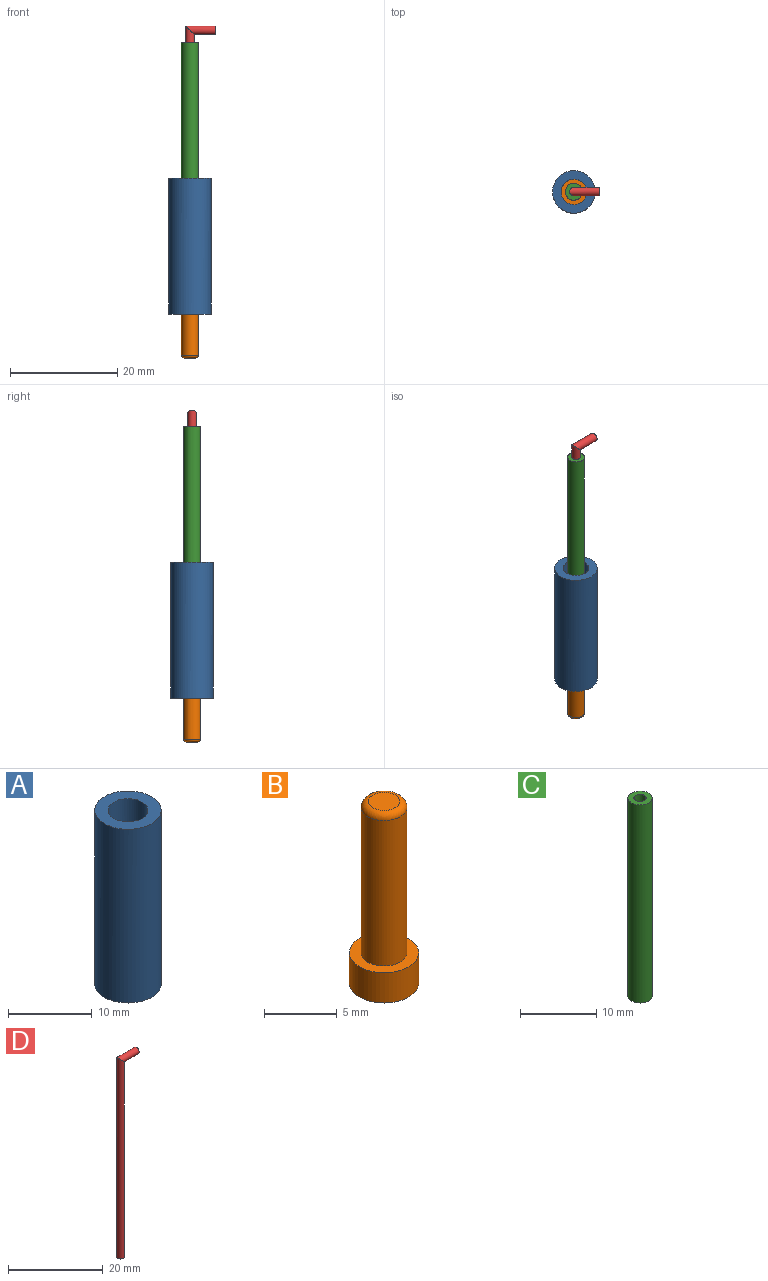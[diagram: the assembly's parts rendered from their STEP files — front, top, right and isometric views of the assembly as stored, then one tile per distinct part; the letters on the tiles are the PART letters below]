
ASSEMBLY  parts=4 mates=3
PART A: 6 faces, bbox 7.9x7.9x25.4 mm
  f0: cylinder r=2.38mm len=22.86mm, axis (0,0,-1), area 342mm2, adj f2,f4
  f1: cylinder r=3.97mm len=25.4mm, axis (0,0,-1), area 633.4mm2, adj f2,f3
  f2: plane 7.94x7.94mm, normal (0,0,1), area 31.7mm2, adj f0,f1
  f3: plane 7.94x7.94mm, normal (0,0,-1), area 41.6mm2, adj f1,f5
  f4: plane 4.76x4.76mm, normal (0,0,1), area 9.9mm2, adj f0,f5
  f5: cylinder r=1.59mm len=3.18mm, axis (0,0,-1), area 25.3mm2, adj f3,f4
PART B: 8 faces, bbox 4.8x4.8x15.2 mm
  f0: cylinder r=2.37mm len=4.75mm, axis (0,0,-1), area 37.9mm2, adj f1,f2
  f1: plane 4.75x4.75mm, normal (0,0,1), area 9.9mm2, adj f0,f3
  f2: plane 4.75x4.75mm, normal (0,0,-1), area 15.7mm2, adj f0,f6
  f3: cylinder r=1.57mm len=12.19mm, axis (0,0,-1), area 120.6mm2, adj f1,f5
  f4: plane 2.13x2.13mm, normal (0,0,1), area 3.6mm2, adj f5
  f5: torus R=1.07mm, axis (0,0,1), area 7mm2, adj f3,f4
  f6: cylinder r=0.79mm len=6.86mm, axis (0,0,-1), area 34.2mm2, adj f2,f7
  f7: plane 1.59x1.59mm, normal (0,0,-1), area 2mm2, adj f6
PART C: 4 faces, bbox 3.2x3.2x31.8 mm
  f0: cylinder r=0.79mm len=31.75mm, axis (0,0,-1), area 158.3mm2, adj f2,f3
  f1: cylinder r=1.59mm len=31.75mm, axis (0,0,-1), area 316.7mm2, adj f2,f3
  f2: plane 3.18x3.18mm, normal (0,0,1), area 5.9mm2, adj f0,f1
  f3: plane 3.18x3.18mm, normal (0,0,-1), area 5.9mm2, adj f0,f1
PART D: 4 faces, bbox 5.6x1.6x51.8 mm
  f0: plane 1.59x1.59mm, normal (1,0,0), area 2mm2, adj f2
  f1: plane 1.59x1.59mm, normal (0,0,-1), area 2mm2, adj f3
  f2: cylinder r=0.79mm len=5.56mm, axis (1,0,0), area 23.8mm2, adj f0,f3
  f3: cylinder r=0.79mm len=51.85mm, axis (0,0,1), area 254.6mm2, adj f1,f2
PLACE A t=(0,0,-12.7)mm
PLACE B rot(axis=(-1,0,0),180deg) t=(0,0,-5.66)mm
PLACE C t=(0,0,6.35)mm
PLACE D t=(0,0,-10.74)mm
MATE fastened A.f0 <-> C.f0  axis (0,0,1) through (0,0,12.7)mm
MATE slider B.f3 <-> A.f5  axis (0,0,-1) through (0,0,-10.74)mm
MATE fastened B.f3 <-> D.f3  axis (0,0,-1) through (0,0,-10.74)mm
